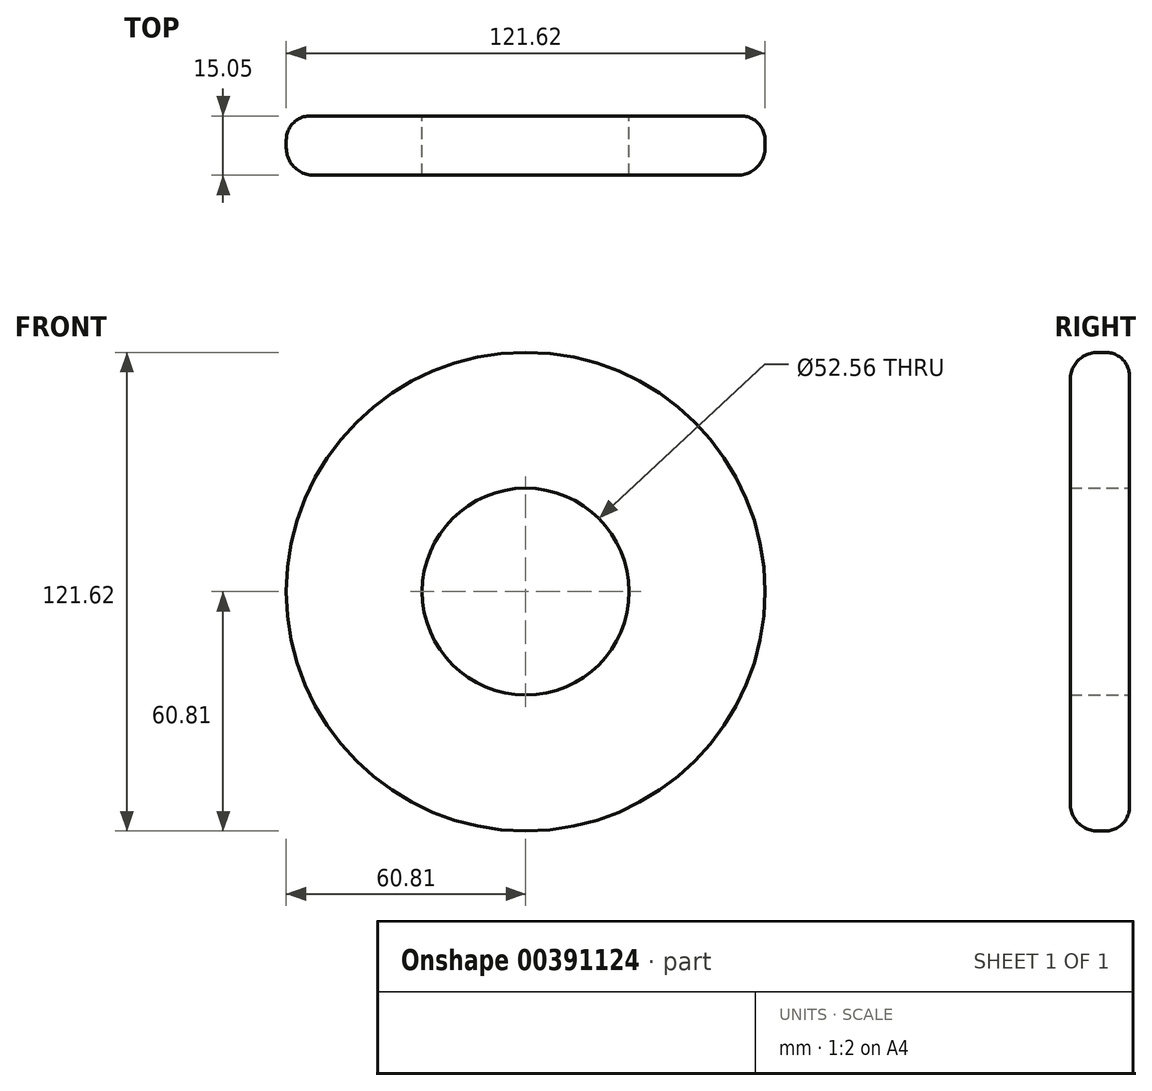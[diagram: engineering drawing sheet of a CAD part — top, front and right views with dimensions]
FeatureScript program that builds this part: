
annotation { "Feature Type Name" : "Feature", "Feature Type Description" : "" }
export const myFeature = defineFeature(function(context is Context, id is Id, definition is map)
    precondition{}
    {
        {
            var Q0;
            Q0=qCreatedBy(makeId("Front.planeOp"),FACE);
            var sketch = newSketch(context, id + "F0", { "sketchPlane" : qUnion([Q0])});
            skLineSegment(sketch, "E0.bottom", {"start": v(-75.92, 74.54) * mm, "end": v(80.17, 74.54) * mm});
            skLineSegment(sketch, "E0.top", {"start": v(-75.92, -79.9) * mm, "end": v(80.17, -79.9) * mm});
            skLineSegment(sketch, "E0.left", {"start": v(-75.92, 74.54) * mm, "end": v(-75.92, -79.9) * mm});
            skLineSegment(sketch, "E0.right", {"start": v(80.17, 74.54) * mm, "end": v(80.17, -79.9) * mm});
            skSolve(sketch);
        }
        {
            var Q0;
            Q0=makeQuery(id+"F0.imprint","IMPRINT",FACE,{"disambiguationData":[TD([[makeQuery(id+"F0.imprint","IMPRINT",EDGE,{"derivedFrom":sQuery(id+"F0.wireOp",EDGE,"E0.bottom")}),-1.0]])]});
            var sketch = newSketch(context, id + "F1", { "sketchPlane" : qUnion([Q0])});
            skCircle(sketch, "E1", {"center": v(0, 0) * mm, "radius": 60.81 * mm});
            skSolve(sketch);
        }
        {
            var Q0;
            Q0 = qBodyType(qCreatedBy(id + "F1" ,EDGE), BodyType.WIRE);
            var sketch = newSketch(context, id + "F2", { "sketchPlane" : qUnion([Q0])});
            skSolve(sketch);
        }
        {
            var Q0;
            Q0 = qSketchRegion(id + "F2", true);
            var Q1;
            Q1=makeQuery(id+"F1.imprint","IMPRINT",FACE,{"disambiguationData":[TD([[makeQuery(id+"F1.imprint","IMPRINT",EDGE,{"derivedFrom":sQuery(id+"F1.wireOp",EDGE,"E1")}),1.0]])]});
            extrude(context, id + "F3", {"entities" : qUnion([Q0, Q1]), "depth" : 15.05 * mm});
        }
        {
            var Q0;
            Q0=makeQuery(id+"F0.imprint","IMPRINT",FACE,{"disambiguationData":[TD([[makeQuery(id+"F0.imprint","IMPRINT",EDGE,{"derivedFrom":sQuery(id+"F0.wireOp",EDGE,"E0.bottom")}),-1.0]])]});
            var sketch = newSketch(context, id + "F4", { "sketchPlane" : qUnion([Q0])});
            skCircle(sketch, "E2", {"center": v(0, 0) * mm, "radius": 26.28 * mm});
            skSolve(sketch);
        }
        {
            var Q0;
            Q0=makeQuery(id+"F4.imprint","IMPRINT",FACE,{"disambiguationData":[TD([[makeQuery(id+"F4.imprint","IMPRINT",EDGE,{"derivedFrom":sQuery(id+"F4.wireOp",EDGE,"E2")}),1.0]])]});
            extrude(context, id + "F5", {"entities" : qUnion([Q0]), "operationType" : NewBodyOperationType.REMOVE, "depth" : 160.92 * mm});
        }
        {
            var Q0;
            Q0=makeQuery(id+"F3.opExtrude","CAP_EDGE",EDGE,{"disambiguationData":[OSD([sQuery(id+"F1.wireOp",EDGE,"E1")])],"isStart":true});
            fillet(context, id + "F6", {"entities" : qUnion([Q0]), "radius" : 6.1 * mm, "tangentPropagation" : true, "allowEdgeOverflow" : false});
        }
        {
            var Q0;
            Q0=makeQuery(id+"F3.opExtrude","CAP_EDGE",EDGE,{"disambiguationData":[OSD([sQuery(id+"F1.wireOp",EDGE,"E1")])],"isStart":false});
            fillet(context, id + "F7", {"entities" : qUnion([Q0]), "radius" : 6.94 * mm, "tangentPropagation" : true, "allowEdgeOverflow" : false});
        }
    });
